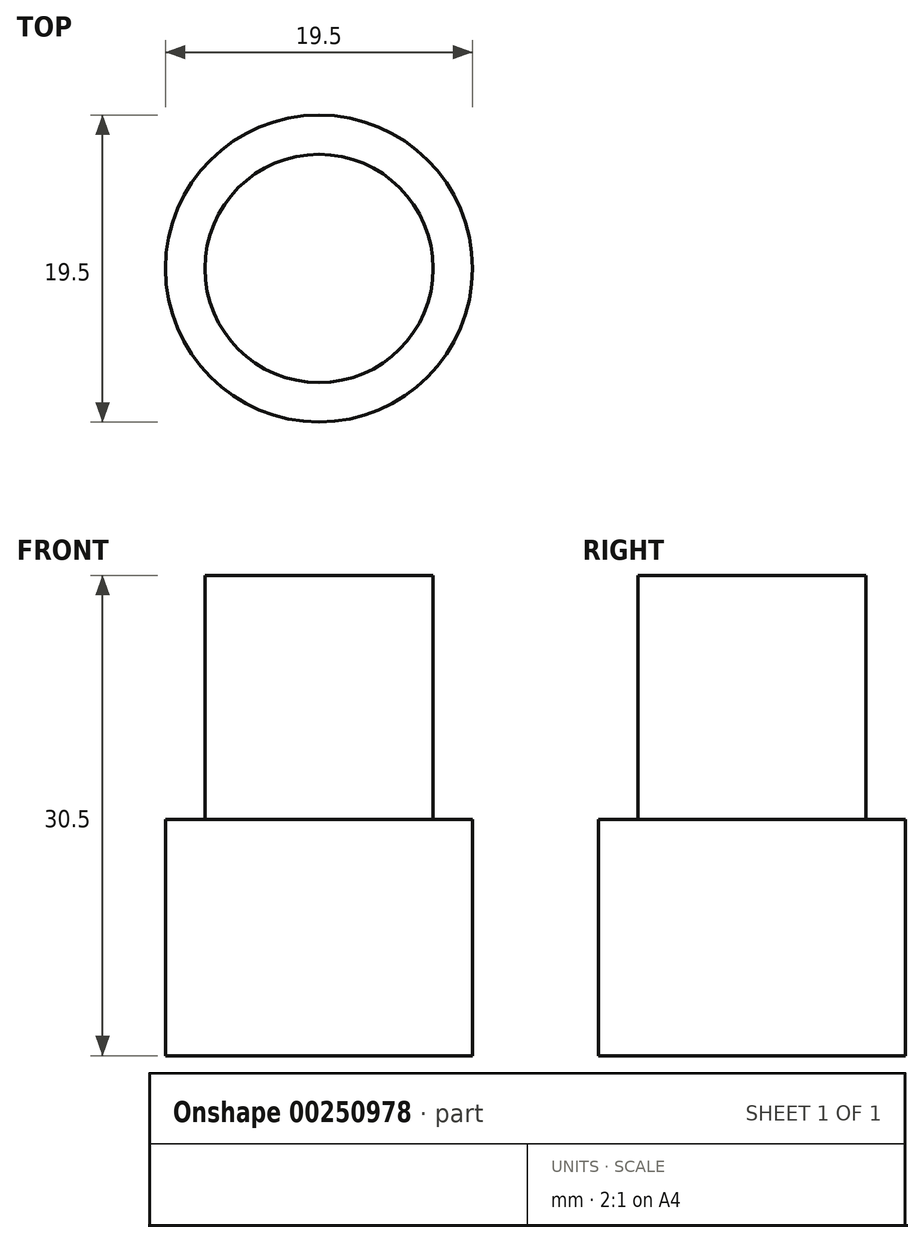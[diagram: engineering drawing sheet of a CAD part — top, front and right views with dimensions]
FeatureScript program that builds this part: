
annotation { "Feature Type Name" : "Feature", "Feature Type Description" : "" }
export const myFeature = defineFeature(function(context is Context, id is Id, definition is map)
    precondition{}
    {
        {
            var Q0;
            Q0=qCreatedBy(makeId("Front.planeOp"),FACE);
            var sketch = newSketch(context, id + "F0", { "sketchPlane" : qUnion([Q0])});
            skLineSegment(sketch, "E0.bottom", {"start": v(9.75, 7.5) * mm, "end": v(-9.75, 7.5) * mm});
            skLineSegment(sketch, "E0.top", {"start": v(9.75, -7.5) * mm, "end": v(-9.75, -7.5) * mm});
            skLineSegment(sketch, "E0.left", {"start": v(9.75, 7.5) * mm, "end": v(9.75, -7.5) * mm});
            skLineSegment(sketch, "E0.right", {"start": v(-9.75, 7.5) * mm, "end": v(-9.75, -7.5) * mm});
            skPoint(sketch, "E0.middle", {"position": v(0, 0) * mm});
            skLineSegment(sketch, "E1", {"start": v(0, 7.5) * mm, "end": v(0, -7.5) * mm});
            skLineSegment(sketch, "E2", {"start": v(0, -7.5) * mm, "end": v(0, 7.5) * mm});
            skSolve(sketch);
        }
        {
            var Q0;
            {var subQ0=sQuery(id+"F0.wireOp",EDGE,"E0.right");Q0=makeQuery(id+"F0.imprint","IMPRINT",FACE,{"disambiguationData":[TD([[makeQuery(id+"F0.imprint","IMPRINT",EDGE,{"derivedFrom":subQ0}),1.0]])]});}
            var Q1;
            Q1=sQuery(id+"F0.wireOp",EDGE,"E2");
            revolve(context, id + "F1", {"entities" : qUnion([Q0]), "axis" : qUnion([Q1]), "revolveType" : RevolveType.FULL});
        }
        {
            var Q0;
            Q0=makeQuery(id+"F1.opRevolve","SWEPT_FACE",FACE,{"disambiguationData":[OSD([sQuery(id+"F0.wireOp",EDGE,"E0.bottom")])]});
            shell(context, id + "F2", {"entities" : qUnion([Q0]), "thickness" : 2.5 * mm});
        }
        {
            var Q0;
            Q0=makeQuery(id+"F2.opShell","OFFSET_FACE",FACE,{"disambiguationData":[OSD([sQuery(id+"F0.wireOp",EDGE,"E0.top")])]});
            extrude(context, id + "F3", {"entities" : qUnion([Q0]), "operationType" : NewBodyOperationType.ADD, "depth" : 28 * mm});
        }
    });
